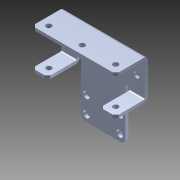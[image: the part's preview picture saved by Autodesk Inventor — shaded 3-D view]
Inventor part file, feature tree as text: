
AUTODESK INVENTOR PART (.ipt)
format: ipt  version: 2014 (Build 180170000, 170)  size: 170,496 bytes
history: native  units: in
note: dims shown in document units (in); Inventor stores cm internally (conversion verified against a paired STEP export)
features: chamfer x1, other x1, imported_body x1
ambient origin geometry x8: Origin, YZ Plane, XZ Plane, XY Plane, X Axis, Y Axis, Z Axis, Center Point
bodies: Body1 (feature_tree)
feature tree (3):
  chamfer  "Chamfer1"  [1 undecoded]
  other  "217-3558-STEP1"
  imported_body  "Base1"
note: 1 required parameter value undecoded (feature->parameter linkage not recoverable at this tier; creation-order binding heuristic only, values carry confidence <= 0.55)
